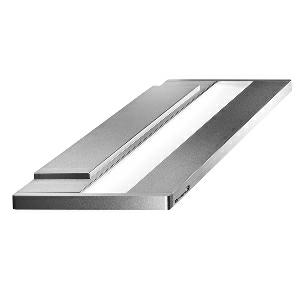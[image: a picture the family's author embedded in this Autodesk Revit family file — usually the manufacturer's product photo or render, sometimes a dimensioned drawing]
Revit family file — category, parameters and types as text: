
# Revit family: zera_bed_-_zew_11000_830_-_ul_00813007_2e9e
name_source: partatom
category: Lighting Fixtures
units: mm (PartAtom-declared; Revit-internal decimal feet)

## family parameters
Cut with Voids When Loaded = No
Host = Face
Light Source = No
Part Type = Normal
Room Calculation Point = No
Round Connector Dimension = Use Diameter
Shared = No

## types (1)
- AL+UL (1 x LED, 9800 lm, 4000K/3000K)
    Apparent Load = 109 VA
    Approval mark = CE
    CIE Flux Codes = 45 81 99 47 100
    Color Rendering = 90/80
    Color Temperature = 4000K/3000K
    Default Elevation = 2000 mm  [stored 6.56168 ft]
    Description = ZEW 11000/830|Wall-mounted luminaire|light source:   Warm white   |work equipment: Power supply unit|luminous flux: 10700 lm|light distribution: Direct/indirect|class of protection: I|technology: Switchable|mains lead: Connector 5 pin|glare control: Diffusor|special features: General light, indirect, 3000K, Ra80, DIN EN 60598-2-25, Reading light, direct, 2700K, Ra90, dir 4K 60W Ra95|
    Frequency = 50 Hz, 60 Hz
    Height = 20 mm  [stored 0.0656168 ft]
    Lamp = 1 x LED
    Lamp Light Flux = 9800 lm
    Lamp count = 1
    Length = 1050 mm
    Luminous efficacy = 90 lm/W
    Manufacturer = Waldmann
    ModVariant = No
    Model = 00813007
    Mounting Place = Wall
    Mounting Type = Surface mounted
    Number of Poles = 1
    OnlyDefault = Yes
    Power Factor = 1
    Product Name = ZERA.bed - ZEW 11000/830 - UL
    Product group = Wall mounted Luminaire
    ProductGroupID = 20
    Protection Class = Protection class I
    Protection Degree = IP 20
    RLX_Detail_Level = 1
    RLX_Emergency_Light_Flux = 0 lm
    RLX_Emergency_Type = 0
    RLX_Emergency_Type_DB = No
    RlxData = <blob elided: 59981 chars, md5=bda07c84>
    Socket = socket
    Standby Power = 0 W
    System Light Flux = 9800 lm
    System Power = 109 W
    Type Comments = General and Examation Light
    Type Image = zera_bed.jpg
    URL = http://relux.com
    VarID = al_ul_37f9
    Voltage = 230 V
    Voltage Range = 220-240 V
    Weight = 0.00 kg
    Width = 230 mm

note: [stored X ft] marks values corroborated as IEEE doubles in the binary element streams (Revit-internal decimal feet)

## geometry (parser evidence)
native form markers: Blend x4, Sweep x14
no freeform markers — native parametric forms only
